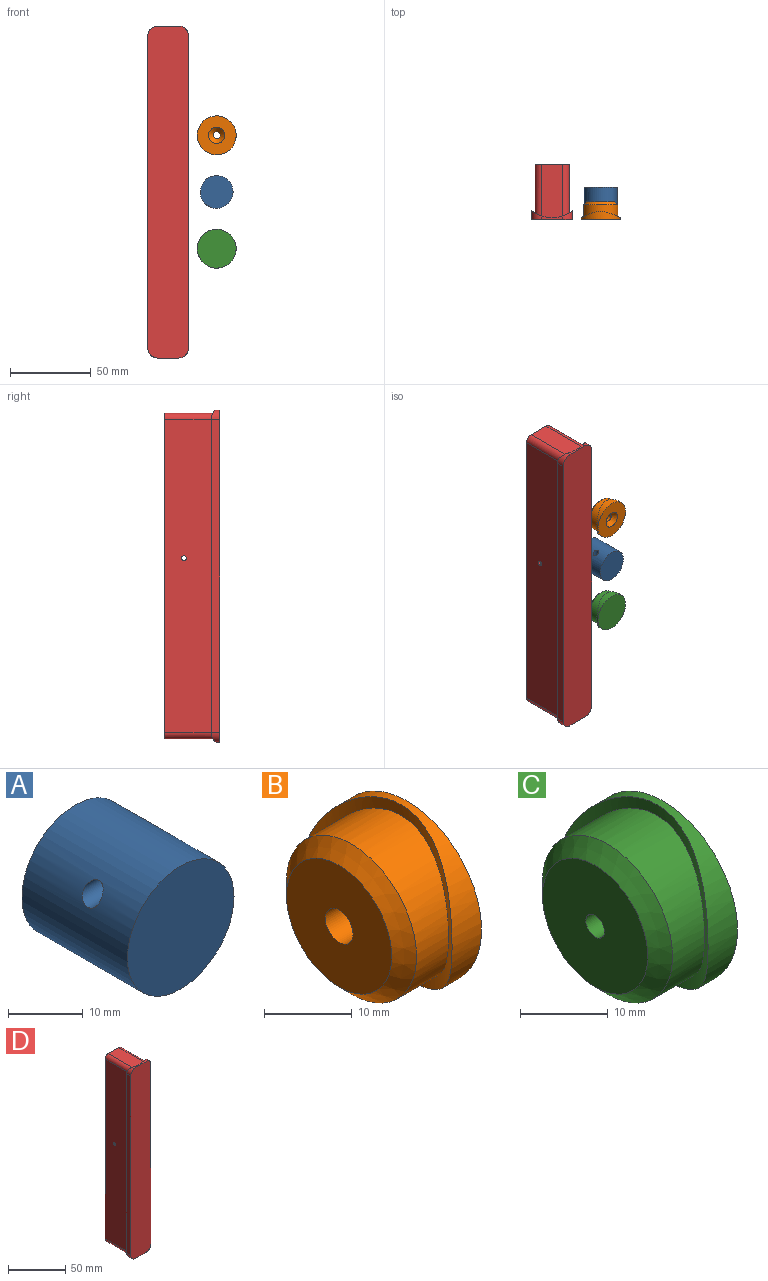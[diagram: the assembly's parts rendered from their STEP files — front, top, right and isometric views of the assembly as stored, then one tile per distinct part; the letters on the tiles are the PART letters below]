
ASSEMBLY  parts=4 mates=3
PART A: 4 faces, bbox 20.2x20x20.2 mm
  f0: cylinder r=10.1mm len=20.2mm, axis (0,1,0), area 1248.6mm2, adj f1,f2,f3
  f1: plane 20.2x20.2mm, normal (0,-1,0), area 320.5mm2, adj f0
  f2: plane 20.2x20.2mm, normal (0,1,0), area 320.5mm2, adj f0
  f3: cylinder r=1.65mm len=18.68mm, axis (1,0,0), area 173.2mm2, adj f0
PART B: 8 faces, bbox 11x24x24 mm
  f0: cylinder r=21mm len=24mm, axis (0,0,1), area 115.5mm2, adj f1,f4
  f1: cylinder r=12mm len=24mm, axis (-1,0,0), area 213.9mm2, adj f0,f2
  f2: plane 24x24mm, normal (1,0,0), area 373.8mm2, adj f1,f7
  f3: plane 17x17mm, normal (-1,0,0), area 211.1mm2, adj f5,f6
  f4: cylinder r=10.5mm len=21mm, axis (1,0,0), area 436.6mm2, adj f0,f5
  f5: cone r=10.5mm half-angle=45deg, axis (1,0,0), area 168.8mm2, adj f3,f4
  f6: cylinder r=2.25mm len=8.25mm, axis (1,0,0), area 116.6mm2, adj f3,f7
  f7: cone r=2.25mm half-angle=45deg, axis (1,0,0), area 88.6mm2, adj f2,f6
PART C: 8 faces, bbox 11x24x24 mm
  f0: cylinder r=21mm len=24mm, axis (0,0,1), area 115.5mm2, adj f1,f4
  f1: cylinder r=12mm len=24mm, axis (-1,0,0), area 213.9mm2, adj f0,f2
  f2: plane 24x24mm, normal (1,0,0), area 452.4mm2, adj f1
  f3: plane 17x17mm, normal (-1,0,0), area 219.9mm2, adj f5,f6
  f4: cylinder r=10.5mm len=21mm, axis (1,0,0), area 436.6mm2, adj f0,f5
  f5: cone r=10.5mm half-angle=45deg, axis (1,0,0), area 168.8mm2, adj f3,f4
  f6: cylinder r=1.5mm len=8mm, axis (-1,0,0), area 75.4mm2, adj f3,f7
  f7: cone r=0mm half-angle=59deg, axis (-1,0,0), area 8.2mm2, adj f6
PART D: 23 faces, bbox 25x34x205 mm
  f0: cylinder r=10.25mm len=30.3mm, axis (0,1,0), area 1934.5mm2, adj f16,f20,f21,f22
  f1: plane 193x5.13mm, normal (-1,0,0), area 989.2mm2, adj f2,f8,f9,f10
  f2: cylinder r=6mm len=6mm, axis (0,1,0), area 36.1mm2, adj f1,f3,f9,f10
  f3: plane 13x2.03mm, normal (0,0,-1), area 17.4mm2, adj f2,f4,f9,f10
  f4: cylinder r=6mm len=6mm, axis (0,1,0), area 36.1mm2, adj f3,f5,f9,f10
  f5: plane 193x5.13mm, normal (1,0,0), area 989.2mm2, adj f4,f6,f9,f10
  f6: cylinder r=6mm len=6mm, axis (0,1,0), area 36.1mm2, adj f5,f7,f9,f10
  f7: plane 13x2.03mm, normal (0,0,1), area 17.4mm2, adj f6,f8,f9,f10
  f8: cylinder r=6mm len=6mm, axis (0,1,0), area 36.1mm2, adj f1,f7,f9,f10
  f9: plane 205x25mm, normal (0,-1,0), area 5094.1mm2, adj f1,f2,f3,f4,f5,f6,f7,f8
  f10: cylinder r=21mm len=205mm, axis (0,0,1), area 1048mm2, adj f1,f2,f3,f4,f5,f6,f7,f8
  f11: plane 33x13mm, normal (0,0,1), area 424.6mm2, adj f10,f12,f16,f18
  f12: cylinder r=4mm len=31.97mm, axis (0,-1,0), area 194.2mm2, adj f10,f11,f13,f16
  f13: plane 193x30.19mm, normal (-1,0,0), area 5818.9mm2, adj f10,f12,f14,f16,f21
  f14: cylinder r=4mm len=31.97mm, axis (0,-1,0), area 194.2mm2, adj f10,f13,f15,f16
  f15: plane 33x13mm, normal (0,0,-1), area 424.6mm2, adj f10,f14,f16,f17
  f16: plane 201x21mm, normal (0,1,0), area 3877.2mm2, adj f0,f11,f12,f13,f14,f15,f17,f18
  f17: cylinder r=4mm len=31.97mm, axis (0,-1,0), area 194.2mm2, adj f10,f15,f16,f19
  f18: cylinder r=4mm len=31.97mm, axis (0,-1,0), area 194.2mm2, adj f10,f11,f16,f19
  f19: plane 193x30.19mm, normal (1,0,0), area 5818.9mm2, adj f10,f16,f17,f18,f22
  f20: plane 20.5x20.5mm, normal (0,1,0), area 330.1mm2, adj f0
  f21: cylinder r=1.5mm len=3.01mm, axis (-1,0,0), area 18.3mm2, adj f0,f13
  f22: cylinder r=1.5mm len=3.01mm, axis (-1,0,0), area 18.3mm2, adj f0,f19
PLACE A rot(axis=(0,-1,0),90deg) t=(30,14,0)mm
PLACE B rot(axis=(0.58,-0.58,-0.58),120deg) t=(30,-1,35)mm
PLACE C rot(axis=(0.58,-0.58,-0.58),120deg) t=(30,-1,-35)mm
PLACE D at identity
MATE fastened B.f1 <-> A.f1  axis (0,-1,0) through (30,-6,35)mm
MATE fastened A.f0 <-> D.f9  axis (0,-1,0) through (30,-6,0)mm
MATE fastened C.f1 <-> A.f1  axis (0,-1,0) through (30,-6,-35)mm
